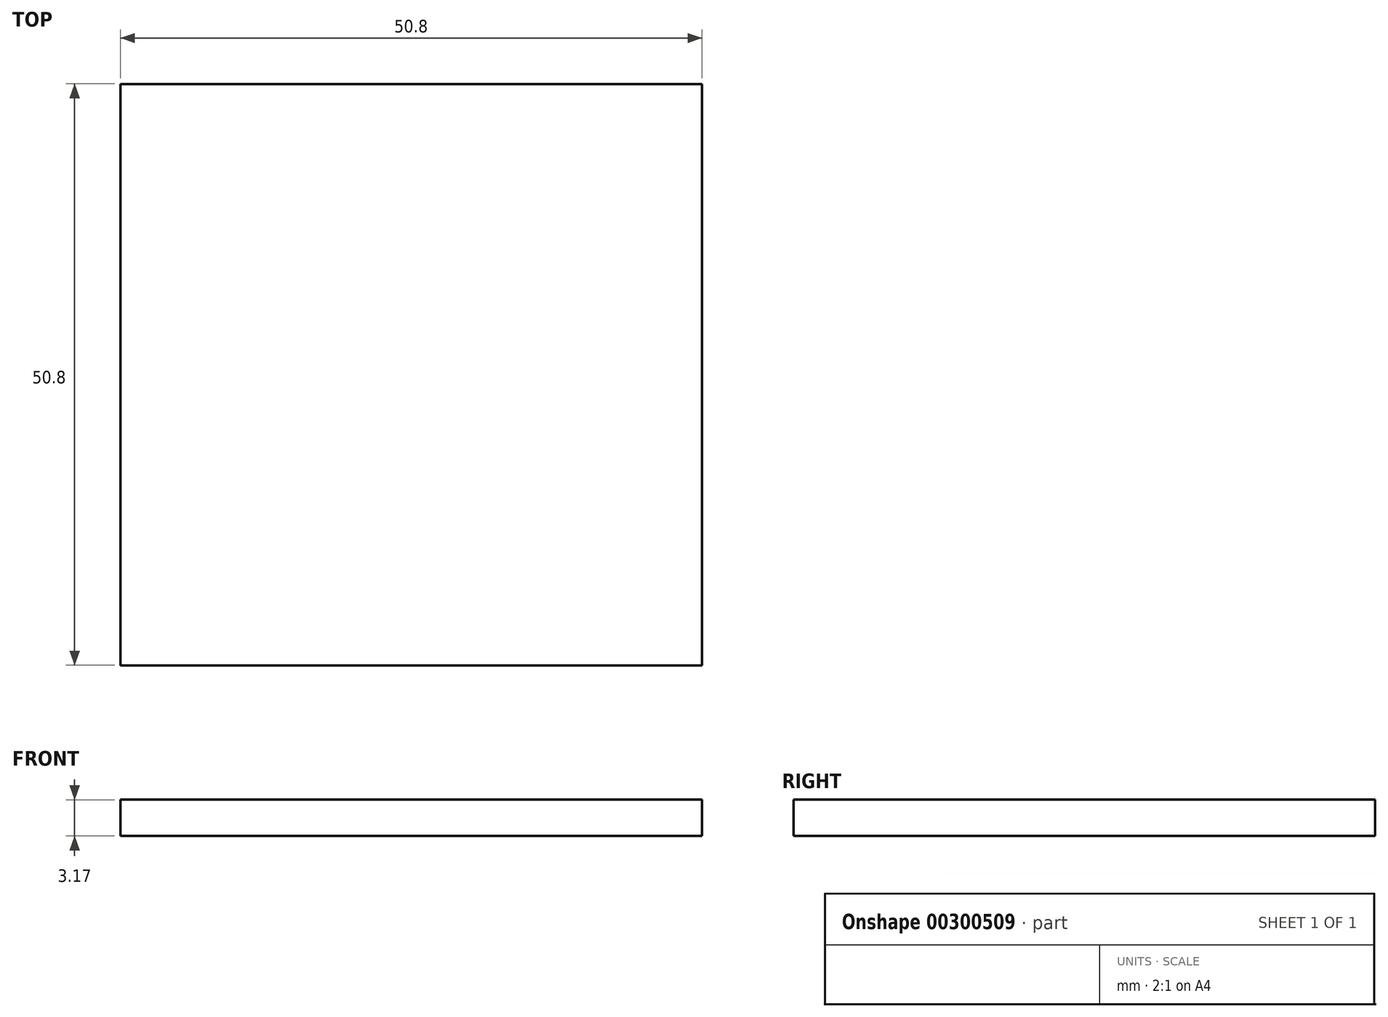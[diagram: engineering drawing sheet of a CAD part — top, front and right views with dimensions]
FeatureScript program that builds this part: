
annotation { "Feature Type Name" : "Feature", "Feature Type Description" : "" }
export const myFeature = defineFeature(function(context is Context, id is Id, definition is map)
    precondition{}
    {
        {
            var Q0;
            Q0=qCreatedBy(makeId("Top.planeOp"),FACE);
            var sketch = newSketch(context, id + "F0", { "sketchPlane" : qUnion([Q0])});
            skLineSegment(sketch, "E0.bottom", {"start": v(-6.76, 37.1) * mm, "end": v(44.04, 37.1) * mm});
            skLineSegment(sketch, "E0.top", {"start": v(-6.76, -13.7) * mm, "end": v(44.04, -13.7) * mm});
            skLineSegment(sketch, "E0.left", {"start": v(-6.76, 37.1) * mm, "end": v(-6.76, -13.7) * mm});
            skLineSegment(sketch, "E0.right", {"start": v(44.04, 37.1) * mm, "end": v(44.04, -13.7) * mm});
            skSolve(sketch);
        }
        {
            var Q0;
            Q0 = qSketchRegion(id + "F0", true);
            extrude(context, id + "F1", {"entities" : qUnion([Q0]), "depth" : 3.17 * mm});
        }
    });
